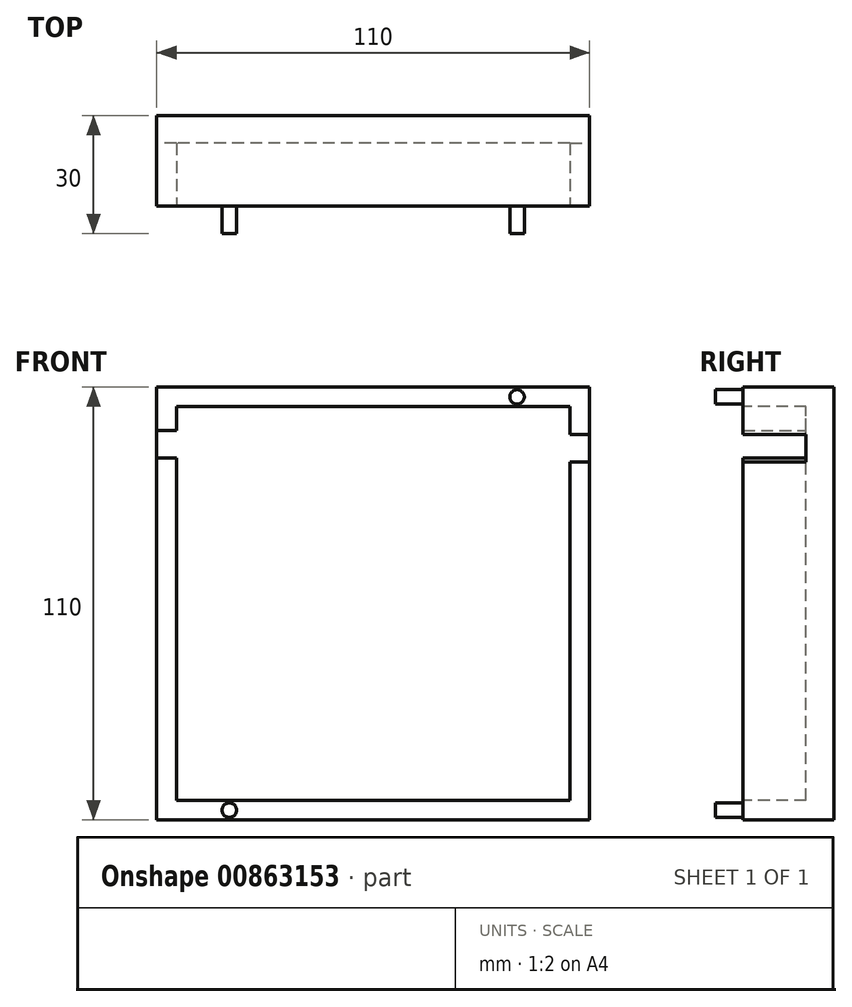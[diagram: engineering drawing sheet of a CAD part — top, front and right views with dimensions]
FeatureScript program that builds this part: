
annotation { "Feature Type Name" : "Feature", "Feature Type Description" : "" }
export const myFeature = defineFeature(function(context is Context, id is Id, definition is map)
    precondition{}
    {
        {
            var Q0;
            Q0=qCreatedBy(makeId("Front.planeOp"),FACE);
            var sketch = newSketch(context, id + "F0", { "sketchPlane" : qUnion([Q0])});
            skLineSegment(sketch, "E0.bottom", {"start": v(55, -55) * mm, "end": v(-55, -55) * mm});
            skLineSegment(sketch, "E0.top", {"start": v(55, 55) * mm, "end": v(-55, 55) * mm});
            skLineSegment(sketch, "E0.left", {"start": v(55, -55) * mm, "end": v(55, 55) * mm});
            skLineSegment(sketch, "E0.right", {"start": v(-55, -55) * mm, "end": v(-55, 55) * mm});
            skPoint(sketch, "E0.middle", {"position": v(0, 0) * mm});
            skSolve(sketch);
        }
        {
            var Q0;
            Q0=makeQuery(id+"F0.imprint","IMPRINT",FACE,{"disambiguationData":[TD([[makeQuery(id+"F0.imprint","IMPRINT",EDGE,{"derivedFrom":sQuery(id+"F0.wireOp",EDGE,"E0.bottom")}),-1.0]])]});
            extrude(context, id + "F1", {"entities" : qUnion([Q0]), "depth" : 30 * mm, "offsetDistance" : 25 * mm});
        }
        {
            var Q0;
            Q0=makeQuery(id+"F1.opExtrude","CAP_FACE",FACE,{"disambiguationData":[OSD([sQuery(id+"F0.wireOp",EDGE,"E0.bottom"),sQuery(id+"F0.wireOp",EDGE,"E0.top"),sQuery(id+"F0.wireOp",EDGE,"E0.left"),sQuery(id+"F0.wireOp",EDGE,"E0.right")])],"isStart":false});
            var sketch = newSketch(context, id + "F2", { "sketchPlane" : qUnion([Q0])});
            skLineSegment(sketch, "E1.bottom", {"start": v(50, -50) * mm, "end": v(-50, -50) * mm});
            skLineSegment(sketch, "E1.top", {"start": v(50, 50) * mm, "end": v(-50, 50) * mm});
            skLineSegment(sketch, "E1.left", {"start": v(50, -50) * mm, "end": v(50, 50) * mm});
            skLineSegment(sketch, "E1.right", {"start": v(-50, -50) * mm, "end": v(-50, 50) * mm});
            skPoint(sketch, "E1.middle", {"position": v(0, 0) * mm});
            skSolve(sketch);
        }
        {
            var Q0;
            Q0=makeQuery(id+"F2.imprint","IMPRINT",FACE,{"disambiguationData":[TD([[makeQuery(id+"F2.imprint","IMPRINT",EDGE,{"derivedFrom":sQuery(id+"F2.wireOp",EDGE,"E1.bottom")}),-1.0]])]});
            extrude(context, id + "F3", {"entities" : qUnion([Q0]), "operationType" : NewBodyOperationType.REMOVE, "oppositeDirection" : true, "depth" : 23 * mm, "offsetDistance" : 25 * mm});
        }
        {
            var Q0;
            Q0=makeQuery(id+"F1.opExtrude","SWEPT_FACE",FACE,{"disambiguationData":[OSD([sQuery(id+"F0.wireOp",EDGE,"E0.left")])]});
            var sketch = newSketch(context, id + "F4", { "sketchPlane" : qUnion([Q0])});
            skLineSegment(sketch, "E2.bottom", {"start": v(-25, 43) * mm, "end": v(-7, 43) * mm});
            skLineSegment(sketch, "E2.top", {"start": v(-25, 36) * mm, "end": v(-7, 36) * mm});
            skLineSegment(sketch, "E2.left", {"start": v(-25, 43) * mm, "end": v(-25, 36) * mm});
            skLineSegment(sketch, "E2.right", {"start": v(-7, 43) * mm, "end": v(-7, 36) * mm});
            skSolve(sketch);
        }
        {
            var Q0;
            Q0=makeQuery(id+"F4.imprint","IMPRINT",FACE,{"disambiguationData":[TD([[makeQuery(id+"F4.imprint","IMPRINT",EDGE,{"derivedFrom":sQuery(id+"F4.wireOp",EDGE,"E2.bottom")}),-1.0]])]});
            extrude(context, id + "F5", {"entities" : qUnion([Q0]), "operationType" : NewBodyOperationType.REMOVE, "oppositeDirection" : true, "depth" : 10 * mm, "offsetDistance" : 25 * mm});
        }
        {
            var Q0;
            Q0=makeQuery(id+"F1.opExtrude","SWEPT_FACE",FACE,{"disambiguationData":[OSD([sQuery(id+"F0.wireOp",EDGE,"E0.right")])]});
            var sketch = newSketch(context, id + "F6", { "sketchPlane" : qUnion([Q0])});
            skLineSegment(sketch, "E3.bottom", {"start": v(25, 37) * mm, "end": v(7, 37) * mm});
            skLineSegment(sketch, "E3.top", {"start": v(25, 44) * mm, "end": v(7, 44) * mm});
            skLineSegment(sketch, "E3.left", {"start": v(25, 37) * mm, "end": v(25, 44) * mm});
            skLineSegment(sketch, "E3.right", {"start": v(7, 37) * mm, "end": v(7, 44) * mm});
            skPoint(sketch, "E3.middle", {"position": v(16, 40.5) * mm});
            skSolve(sketch);
        }
        {
            var Q0;
            Q0=makeQuery(id+"F6.imprint","IMPRINT",FACE,{"disambiguationData":[TD([[makeQuery(id+"F6.imprint","IMPRINT",EDGE,{"derivedFrom":sQuery(id+"F6.wireOp",EDGE,"E3.bottom")}),-1.0]])]});
            extrude(context, id + "F7", {"entities" : qUnion([Q0]), "operationType" : NewBodyOperationType.REMOVE, "oppositeDirection" : true, "depth" : 10 * mm, "offsetDistance" : 25 * mm});
        }
        {
            var Q0;
            Q0=makeQuery(id+"F1.opExtrude","CAP_FACE",FACE,{"disambiguationData":[OSD([sQuery(id+"F0.wireOp",EDGE,"E0.bottom"),sQuery(id+"F0.wireOp",EDGE,"E0.top"),sQuery(id+"F0.wireOp",EDGE,"E0.left"),sQuery(id+"F0.wireOp",EDGE,"E0.right")])],"isStart":false});
            var sketch = newSketch(context, id + "F8", { "sketchPlane" : qUnion([Q0])});
            skCircle(sketch, "E4", {"center": v(-36.55, 52.5) * mm, "radius": 1.85 * mm});
            skCircle(sketch, "E5.MirrorC", {"center": v(36.55, 52.5) * mm, "radius": 1.85 * mm});
            skCircle(sketch, "E6.MirrorC", {"center": v(36.55, -52.5) * mm, "radius": 1.85 * mm});
            skCircle(sketch, "E7.MirrorC", {"center": v(-36.55, -52.5) * mm, "radius": 1.85 * mm});
            skSolve(sketch);
        }
        {
            var Q0;
            Q0=makeQuery(id+"F8.imprint","IMPRINT",FACE,{"disambiguationData":[TD([[makeQuery(id+"F8.imprint","IMPRINT",EDGE,{"derivedFrom":sQuery(id+"F8.wireOp",EDGE,"E4")}),1.0]])]});
            var Q1;
            Q1=makeQuery(id+"F8.imprint","IMPRINT",FACE,{"disambiguationData":[TD([[makeQuery(id+"F8.imprint","IMPRINT",EDGE,{"derivedFrom":sQuery(id+"F8.wireOp",EDGE,"E5.MirrorC")}),-1.0]])]});
            var Q2;
            Q2=makeQuery(id+"F8.imprint","IMPRINT",FACE,{"disambiguationData":[TD([[makeQuery(id+"F8.imprint","IMPRINT",EDGE,{"derivedFrom":sQuery(id+"F8.wireOp",EDGE,"E7.MirrorC")}),-1.0]])]});
            var Q3;
            Q3=makeQuery(id+"F8.imprint","IMPRINT",FACE,{"disambiguationData":[TD([[makeQuery(id+"F8.imprint","IMPRINT",EDGE,{"derivedFrom":sQuery(id+"F8.wireOp",EDGE,"E6.MirrorC")}),1.0]])]});
            extrude(context, id + "F9", {"entities" : qUnion([Q0, Q1, Q2, Q3]), "operationType" : NewBodyOperationType.REMOVE, "oppositeDirection" : true, "depth" : 7 * mm, "offsetDistance" : 25 * mm});
        }
    });
